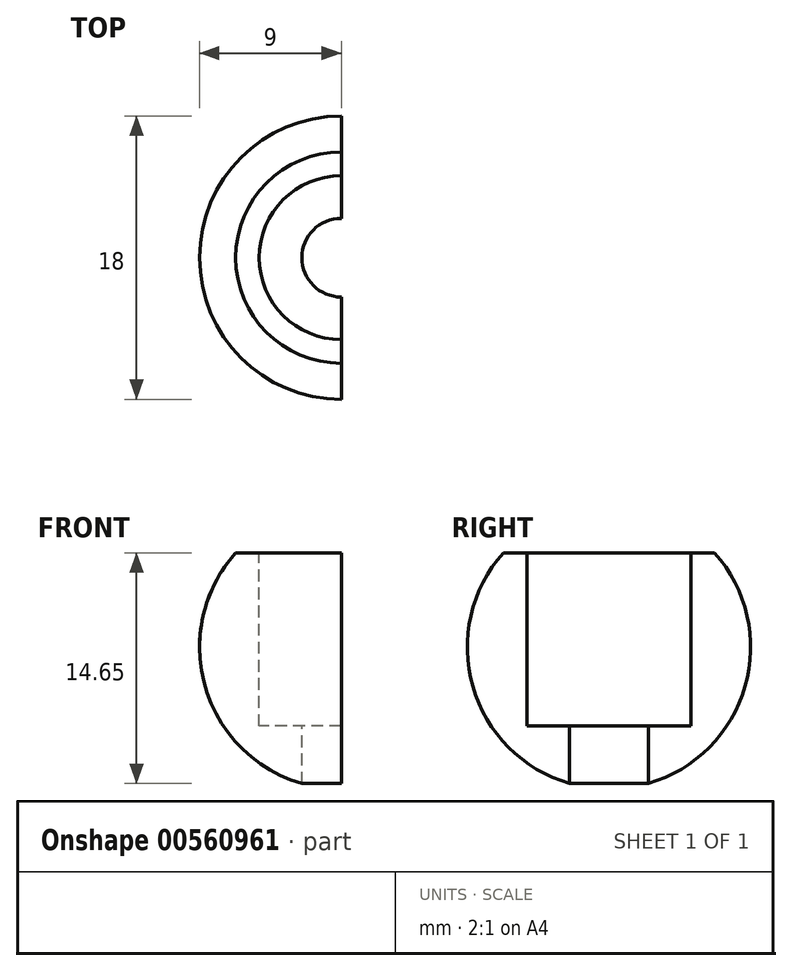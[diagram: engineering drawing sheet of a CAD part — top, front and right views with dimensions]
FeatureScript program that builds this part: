
annotation { "Feature Type Name" : "Feature", "Feature Type Description" : "" }
export const myFeature = defineFeature(function(context is Context, id is Id, definition is map)
    precondition{}
    {
        {
            var Q0;
            Q0=qCreatedBy(makeId("Front.planeOp"),FACE);
            var sketch = newSketch(context, id + "F0", { "sketchPlane" : qUnion([Q0])});
            skLineSegment(sketch, "E0", {"start": v(0, 0) * mm, "end": v(-9, 0) * mm});
            skLineSegment(sketch, "E1", {"start": v(0, 0) * mm, "end": v(0, 9) * mm});
            skArc(sketch, "E2", {"start": v(0, 9) * mm, "mid": v(-6.36, 6.36) * mm, "end": v(-9, 0) * mm});
            skSolve(sketch);
        }
        {
            var Q0;
            Q0=makeQuery(id+"F0.imprint","IMPRINT",FACE,{"disambiguationData":[TD([[makeQuery(id+"F0.imprint","IMPRINT",EDGE,{"derivedFrom":sQuery(id+"F0.wireOp",EDGE,"E0")}),-1.0]])]});
            var Q1;
            Q1=sQuery(id+"F0.wireOp",EDGE,"E0");
            revolve(context, id + "F1", {"entities" : qUnion([Q0]), "axis" : qUnion([Q1]), "revolveType" : RevolveType.FULL});
        }
        {
            var Q0;
            Q0=qCreatedBy(makeId("Top.planeOp"),FACE);
            var sketch = newSketch(context, id + "F2", { "sketchPlane" : qUnion([Q0])});
            skCircle(sketch, "E3", {"center": v(0, 0) * mm, "radius": 2.5 * mm});
            skSolve(sketch);
        }
        {
            var Q0;
            Q0=qSketchRegion(id+"F2",true);
            extrude(context, id + "F3", {"entities" : qUnion([Q0]), "operationType" : NewBodyOperationType.REMOVE, "endBound" : BoundingType.THROUGH_ALL, "oppositeDirection" : true, "depth" : 25 * mm, "offsetDistance" : 25 * mm, "hasSecondDirection" : true, "secondDirectionBound" : BoundingType.THROUGH_ALL, "secondDirectionOppositeDirection" : false, "secondDirectionDepth" : 25 * mm});
        }
        {
            var Q0;
            Q0=qCreatedBy(makeId("Top.planeOp"),FACE);
            cPlane(context, id + "F4", {"entities" : qUnion([Q0]), "cplaneType" : CPlaneType.OFFSET, "offset" : 6 * mm, "width" : 150 * mm, "height" : 150 * mm});
        }
        {
            var Q0;
            Q0=qCreatedBy(id+"F4.planeOp",FACE);
            var sketch = newSketch(context, id + "F5", { "sketchPlane" : qUnion([Q0])});
            skCircle(sketch, "E4", {"center": v(0, 0) * mm, "radius": 13.5 * mm});
            skSolve(sketch);
        }
        {
            var Q0;
            Q0=makeQuery(id+"F5.imprint","IMPRINT",FACE,{"disambiguationData":[TD([[makeQuery(id+"F5.imprint","IMPRINT",EDGE,{"derivedFrom":sQuery(id+"F5.wireOp",EDGE,"E4")}),1.0]])]});
            extrude(context, id + "F6", {"entities" : qUnion([Q0]), "operationType" : NewBodyOperationType.REMOVE, "endBound" : BoundingType.THROUGH_ALL, "depth" : 25 * mm, "offsetDistance" : 25 * mm});
        }
        {
            var Q0;
            {var subQ0=makeQuery(id+"F1.opRevolve","SWEPT_FACE",FACE,{"disambiguationData":[OSD([sQuery(id+"F0.wireOp",EDGE,"E1")])]});Q0=makeQuery(id+"F6.boolean.opBoolean","COPY",FACE,{"disambiguationData":[TD([subQ0])],"derivedFrom":makeQuery(id+"F6.opExtrude","CAP_FACE",FACE,{"disambiguationData":[OSD([sQuery(id+"F5.wireOp",EDGE,"E4")])],"isStart":true})});}
            var sketch = newSketch(context, id + "F7", { "sketchPlane" : qUnion([Q0])});
            skCircle(sketch, "E5", {"center": v(0, 0) * mm, "radius": 5.2 * mm});
            skSolve(sketch);
        }
        {
            var Q0;
            {var subQ1=makeQuery(id+"F6.opExtrude","CAP_FACE",FACE,{"disambiguationData":[OSD([sQuery(id+"F5.wireOp",EDGE,"E4")])],"isStart":true});var subQ2=makeQuery(id+"F1.opRevolve","SWEPT_FACE",FACE,{"disambiguationData":[OSD([sQuery(id+"F0.wireOp",EDGE,"E1")])]});var subQ7=makeQuery(id+"F6.boolean.opBoolean","INTERSECT",EDGE,{"derivedFrom":[makeQuery(id+"F3.boolean.opBoolean","COPY",FACE,{"disambiguationData":[TD([subQ2])],"derivedFrom":makeQuery(id+"F3.opExtrude","SWEPT_FACE",FACE,{"disambiguationData":[OSD([sQuery(id+"F2.wireOp",EDGE,"E3")])]})}),subQ1]});Q0=makeQuery(id+"F7.imprint","IMPRINT",FACE,{"disambiguationData":[TD([[makeQuery(id+"F7.imprint","IMPRINT",EDGE,{"derivedFrom":subQ7}),1.0]])]});}
            var Q1;
            {var subQ1=makeQuery(id+"F6.opExtrude","CAP_FACE",FACE,{"disambiguationData":[OSD([sQuery(id+"F5.wireOp",EDGE,"E4")])],"isStart":true});var subQ2=makeQuery(id+"F1.opRevolve","SWEPT_FACE",FACE,{"disambiguationData":[OSD([sQuery(id+"F0.wireOp",EDGE,"E1")])]});var subQ7=makeQuery(id+"F6.boolean.opBoolean","INTERSECT",EDGE,{"derivedFrom":[makeQuery(id+"F3.boolean.opBoolean","COPY",FACE,{"disambiguationData":[TD([subQ2])],"derivedFrom":makeQuery(id+"F3.opExtrude","SWEPT_FACE",FACE,{"disambiguationData":[OSD([sQuery(id+"F2.wireOp",EDGE,"E3")])]})}),subQ1]});Q1=makeQuery(id+"F7.imprint","IMPRINT",FACE,{"disambiguationData":[TD([[makeQuery(id+"F7.imprint","IMPRINT",EDGE,{"derivedFrom":subQ7}),-1.0]])]});}
            extrude(context, id + "F8", {"entities" : qUnion([Q0, Q1]), "operationType" : NewBodyOperationType.REMOVE, "oppositeDirection" : true, "depth" : 11 * mm, "offsetDistance" : 25 * mm});
        }
    });
